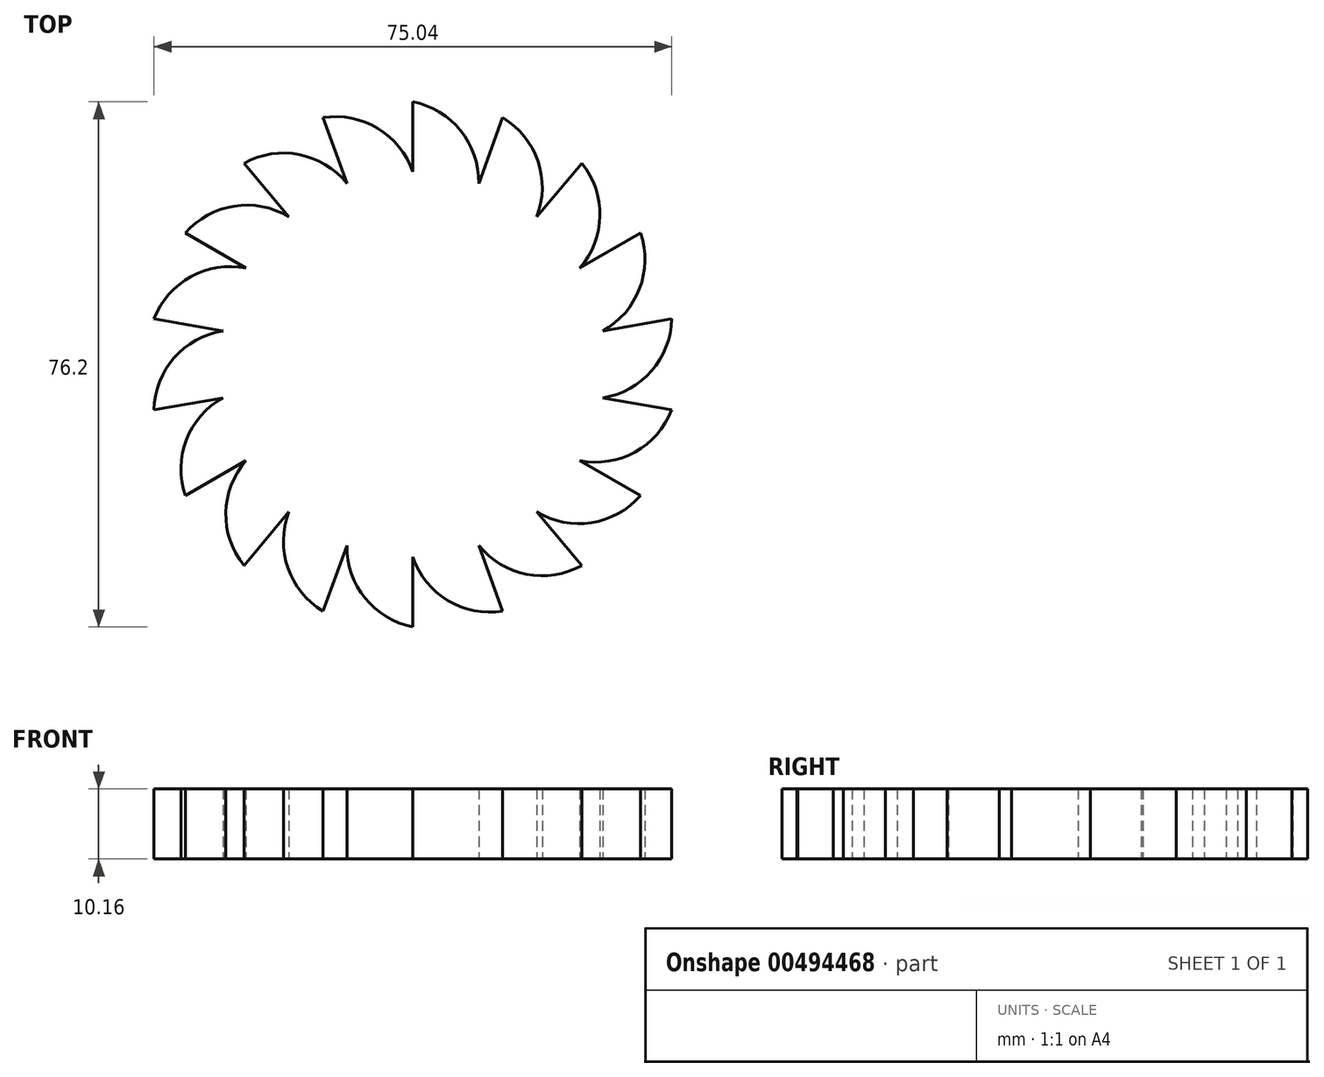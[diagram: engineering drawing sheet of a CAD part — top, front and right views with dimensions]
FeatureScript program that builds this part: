
annotation { "Feature Type Name" : "Feature", "Feature Type Description" : "" }
export const myFeature = defineFeature(function(context is Context, id is Id, definition is map)
    precondition{}
    {
        {
            var Q0;
            Q0=qCreatedBy(makeId("Top.planeOp"),FACE);
            var sketch = newSketch(context, id + "F0", { "sketchPlane" : qUnion([Q0])});
            skPoint(sketch, "E0", {"position": v(0, 38.1) * mm});
            skPoint(sketch, "E1", {"position": v(0, 27.94) * mm});
            skLineSegment(sketch, "E2", {"start": v(0, 38.1) * mm, "end": v(0, 27.94) * mm});
            skLineSegment(sketch, "E3.1.0", {"start": v(-13.03, 35.8) * mm, "end": v(-9.56, 26.26) * mm});
            skPoint(sketch, "E3.1.1", {"position": v(-13.03, 35.8) * mm});
            skPoint(sketch, "E3.1.2", {"position": v(-9.56, 26.26) * mm});
            skLineSegment(sketch, "E3.2.0", {"start": v(-24.5, 29.19) * mm, "end": v(-17.96, 21.4) * mm});
            skPoint(sketch, "E3.2.1", {"position": v(-24.5, 29.19) * mm});
            skPoint(sketch, "E3.2.2", {"position": v(-17.96, 21.4) * mm});
            skLineSegment(sketch, "E3.3.0", {"start": v(-33, 19.05) * mm, "end": v(-24.2, 13.97) * mm});
            skPoint(sketch, "E3.3.1", {"position": v(-33, 19.05) * mm});
            skPoint(sketch, "E3.3.2", {"position": v(-24.2, 13.97) * mm});
            skLineSegment(sketch, "E3.4.0", {"start": v(-37.52, 6.62) * mm, "end": v(-27.52, 4.85) * mm});
            skPoint(sketch, "E3.4.1", {"position": v(-37.52, 6.62) * mm});
            skPoint(sketch, "E3.4.2", {"position": v(-27.52, 4.85) * mm});
            skLineSegment(sketch, "E3.5.0", {"start": v(-37.52, -6.62) * mm, "end": v(-27.52, -4.85) * mm});
            skPoint(sketch, "E3.5.1", {"position": v(-37.52, -6.62) * mm});
            skPoint(sketch, "E3.5.2", {"position": v(-27.52, -4.85) * mm});
            skLineSegment(sketch, "E3.6.0", {"start": v(-33, -19.05) * mm, "end": v(-24.2, -13.97) * mm});
            skPoint(sketch, "E3.6.1", {"position": v(-33, -19.05) * mm});
            skPoint(sketch, "E3.6.2", {"position": v(-24.2, -13.97) * mm});
            skLineSegment(sketch, "E3.7.0", {"start": v(-24.5, -29.19) * mm, "end": v(-17.96, -21.4) * mm});
            skPoint(sketch, "E3.7.1", {"position": v(-24.5, -29.19) * mm});
            skPoint(sketch, "E3.7.2", {"position": v(-17.96, -21.4) * mm});
            skLineSegment(sketch, "E3.8.0", {"start": v(-13.03, -35.8) * mm, "end": v(-9.56, -26.26) * mm});
            skPoint(sketch, "E3.8.1", {"position": v(-13.03, -35.8) * mm});
            skPoint(sketch, "E3.8.2", {"position": v(-9.56, -26.26) * mm});
            skLineSegment(sketch, "E3.9.0", {"start": v(0, -38.1) * mm, "end": v(0, -27.94) * mm});
            skPoint(sketch, "E3.9.1", {"position": v(0, -38.1) * mm});
            skPoint(sketch, "E3.9.2", {"position": v(0, -27.94) * mm});
            skLineSegment(sketch, "E3.10.0", {"start": v(13.03, -35.8) * mm, "end": v(9.56, -26.26) * mm});
            skPoint(sketch, "E3.10.1", {"position": v(13.03, -35.8) * mm});
            skPoint(sketch, "E3.10.2", {"position": v(9.56, -26.26) * mm});
            skLineSegment(sketch, "E3.11.0", {"start": v(24.5, -29.19) * mm, "end": v(17.96, -21.4) * mm});
            skPoint(sketch, "E3.11.1", {"position": v(24.5, -29.19) * mm});
            skPoint(sketch, "E3.11.2", {"position": v(17.96, -21.4) * mm});
            skLineSegment(sketch, "E3.12.0", {"start": v(33, -19.05) * mm, "end": v(24.2, -13.97) * mm});
            skPoint(sketch, "E3.12.1", {"position": v(33, -19.05) * mm});
            skPoint(sketch, "E3.12.2", {"position": v(24.2, -13.97) * mm});
            skLineSegment(sketch, "E3.13.0", {"start": v(37.52, -6.62) * mm, "end": v(27.52, -4.85) * mm});
            skPoint(sketch, "E3.13.1", {"position": v(37.52, -6.62) * mm});
            skPoint(sketch, "E3.13.2", {"position": v(27.52, -4.85) * mm});
            skLineSegment(sketch, "E3.14.0", {"start": v(37.52, 6.62) * mm, "end": v(27.52, 4.85) * mm});
            skPoint(sketch, "E3.14.1", {"position": v(37.52, 6.62) * mm});
            skPoint(sketch, "E3.14.2", {"position": v(27.52, 4.85) * mm});
            skLineSegment(sketch, "E3.15.0", {"start": v(33, 19.05) * mm, "end": v(24.2, 13.97) * mm});
            skPoint(sketch, "E3.15.1", {"position": v(33, 19.05) * mm});
            skPoint(sketch, "E3.15.2", {"position": v(24.2, 13.97) * mm});
            skLineSegment(sketch, "E3.16.0", {"start": v(24.5, 29.19) * mm, "end": v(17.96, 21.4) * mm});
            skPoint(sketch, "E3.16.1", {"position": v(24.5, 29.19) * mm});
            skPoint(sketch, "E3.16.2", {"position": v(17.96, 21.4) * mm});
            skLineSegment(sketch, "E3.17.0", {"start": v(13.03, 35.8) * mm, "end": v(9.56, 26.26) * mm});
            skPoint(sketch, "E3.17.1", {"position": v(13.03, 35.8) * mm});
            skPoint(sketch, "E3.17.2", {"position": v(9.56, 26.26) * mm});
            skPoint(sketch, "E3.center", {"position": v(0, 0) * mm});
            skArc(sketch, "E4", {"start": v(9.56, 26.26) * mm, "mid": v(6.93, 33.92) * mm, "end": v(0, 38.1) * mm});
            skPoint(sketch, "E4.third.point", {"position": v(-10.17, 17.67) * mm});
            skArc(sketch, "E5.1.0", {"start": v(0, 27.94) * mm, "mid": v(-5.08, 34.24) * mm, "end": v(-13.03, 35.8) * mm});
            skArc(sketch, "E5.2.0", {"start": v(-9.56, 26.26) * mm, "mid": v(-16.49, 30.44) * mm, "end": v(-24.5, 29.19) * mm});
            skArc(sketch, "E5.3.0", {"start": v(-17.96, 21.4) * mm, "mid": v(-25.9, 22.96) * mm, "end": v(-33, 19.05) * mm});
            skArc(sketch, "E5.4.0", {"start": v(-24.2, 13.97) * mm, "mid": v(-32.2, 12.72) * mm, "end": v(-37.52, 6.62) * mm});
            skArc(sketch, "E5.5.0", {"start": v(-27.52, 4.85) * mm, "mid": v(-34.6, 0.94) * mm, "end": v(-37.52, -6.62) * mm});
            skArc(sketch, "E5.6.0", {"start": v(-27.52, -4.85) * mm, "mid": v(-32.84, -10.95) * mm, "end": v(-33, -19.05) * mm});
            skArc(sketch, "E5.7.0", {"start": v(-24.2, -13.97) * mm, "mid": v(-27.11, -21.52) * mm, "end": v(-24.5, -29.19) * mm});
            skArc(sketch, "E5.8.0", {"start": v(-17.96, -21.4) * mm, "mid": v(-18.12, -29.5) * mm, "end": v(-13.03, -35.8) * mm});
            skArc(sketch, "E5.9.0", {"start": v(-9.56, -26.26) * mm, "mid": v(-6.93, -33.92) * mm, "end": v(0, -38.1) * mm});
            skArc(sketch, "E5.10.0", {"start": v(0, -27.94) * mm, "mid": v(5.08, -34.24) * mm, "end": v(13.03, -35.8) * mm});
            skArc(sketch, "E5.11.0", {"start": v(9.56, -26.26) * mm, "mid": v(16.49, -30.44) * mm, "end": v(24.5, -29.19) * mm});
            skArc(sketch, "E5.12.0", {"start": v(17.96, -21.4) * mm, "mid": v(25.9, -22.96) * mm, "end": v(33, -19.05) * mm});
            skArc(sketch, "E5.13.0", {"start": v(24.2, -13.97) * mm, "mid": v(32.2, -12.72) * mm, "end": v(37.52, -6.62) * mm});
            skArc(sketch, "E5.14.0", {"start": v(27.52, -4.85) * mm, "mid": v(34.6, -0.94) * mm, "end": v(37.52, 6.62) * mm});
            skArc(sketch, "E5.15.0", {"start": v(27.52, 4.85) * mm, "mid": v(32.84, 10.95) * mm, "end": v(33, 19.05) * mm});
            skArc(sketch, "E5.16.0", {"start": v(24.2, 13.97) * mm, "mid": v(27.11, 21.52) * mm, "end": v(24.5, 29.19) * mm});
            skArc(sketch, "E5.17.0", {"start": v(17.96, 21.4) * mm, "mid": v(18.12, 29.5) * mm, "end": v(13.03, 35.8) * mm});
            skSolve(sketch);
        }
        {
            var Q0;
            Q0=makeQuery(id+"F0.imprint","IMPRINT",FACE,{"disambiguationData":[TD([[makeQuery(id+"F0.imprint","IMPRINT",EDGE,{"derivedFrom":sQuery(id+"F0.wireOp",EDGE,"E2")}),1.0]])]});
            extrude(context, id + "F1", {"entities" : qUnion([Q0]), "depth" : 10.16 * mm});
        }
    });
